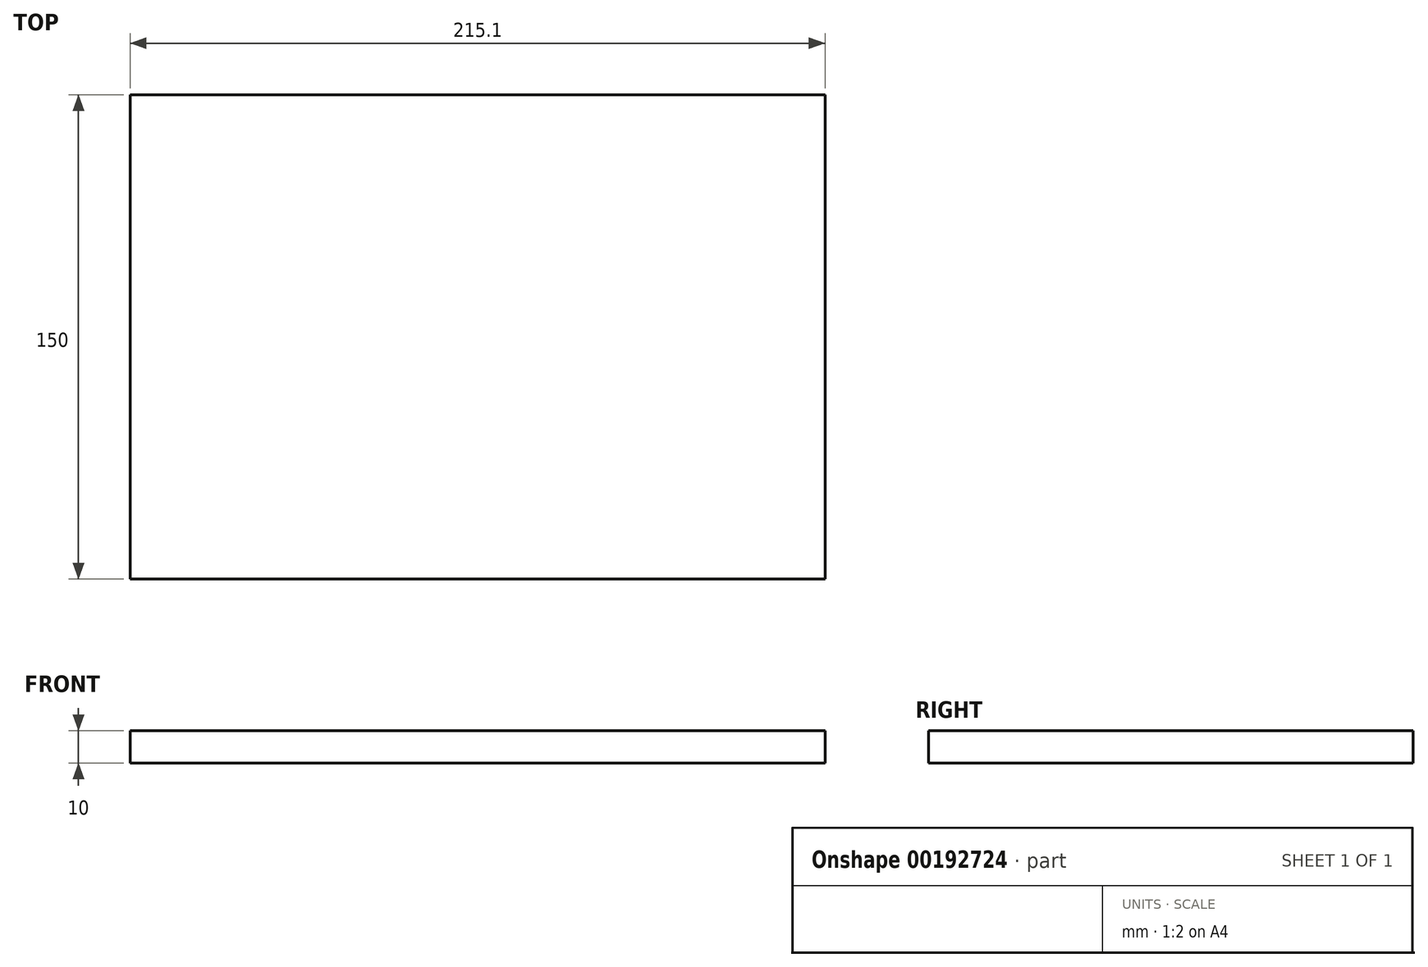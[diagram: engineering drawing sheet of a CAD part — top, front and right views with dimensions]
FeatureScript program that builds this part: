
annotation { "Feature Type Name" : "Feature", "Feature Type Description" : "" }
export const myFeature = defineFeature(function(context is Context, id is Id, definition is map)
    precondition{}
    {
        {
            var Q0;
            Q0=qCreatedBy(makeId("Top.planeOp"),FACE);
            var sketch = newSketch(context, id + "F0", { "sketchPlane" : qUnion([Q0])});
            skLineSegment(sketch, "E0.bottom", {"start": v(107.55, 75) * mm, "end": v(-107.55, 75) * mm});
            skLineSegment(sketch, "E0.top", {"start": v(107.55, -75) * mm, "end": v(-107.55, -75) * mm});
            skLineSegment(sketch, "E0.left", {"start": v(107.55, 75) * mm, "end": v(107.55, -75) * mm});
            skLineSegment(sketch, "E0.right", {"start": v(-107.55, 75) * mm, "end": v(-107.55, -75) * mm});
            skPoint(sketch, "E0.middle", {"position": v(0, 0) * mm});
            skSolve(sketch);
        }
        {
            var Q0;
            Q0 = qSketchRegion(id + "F0", true);
            extrude(context, id + "F1", {"entities" : qUnion([Q0]), "depth" : 10 * mm});
        }
    });
